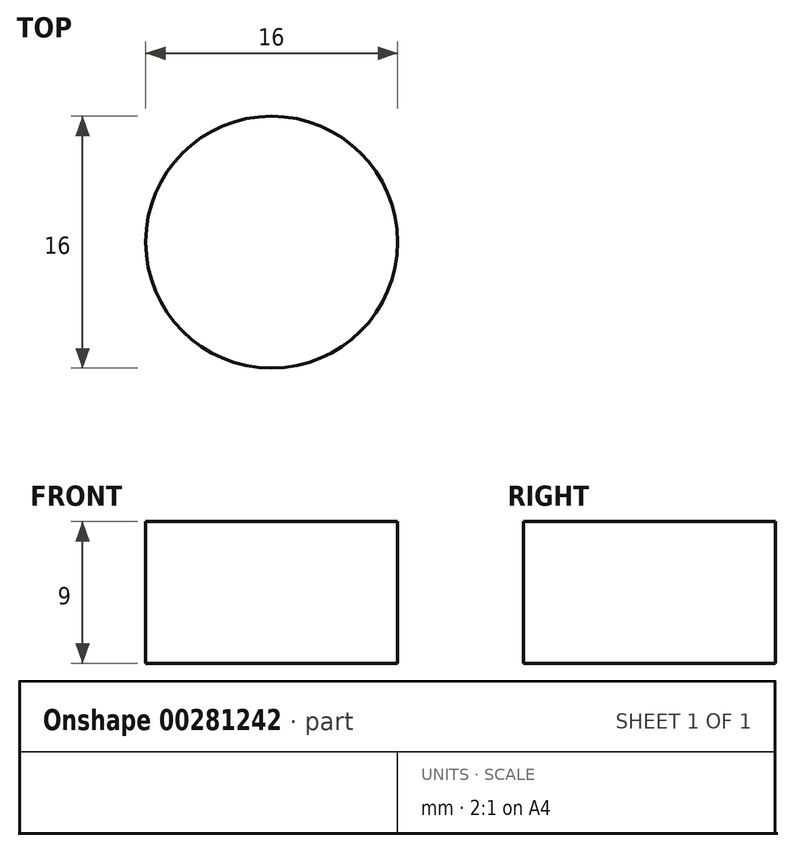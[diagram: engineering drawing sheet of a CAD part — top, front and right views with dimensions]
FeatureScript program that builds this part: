
annotation { "Feature Type Name" : "Feature", "Feature Type Description" : "" }
export const myFeature = defineFeature(function(context is Context, id is Id, definition is map)
    precondition{}
    {
        {
            var Q0;
            Q0=qCreatedBy(makeId("Top.planeOp"),FACE);
            var sketch = newSketch(context, id + "F0", { "sketchPlane" : qUnion([Q0])});
            skCircle(sketch, "E0", {"center": v(0, 0) * mm, "radius": 8 * mm});
            skSolve(sketch);
        }
        {
            var Q0;
            Q0=qSketchRegion(id+"F0",true);
            extrude(context, id + "F1", {"entities" : qUnion([Q0]), "depth" : 9 * mm});
        }
    });
